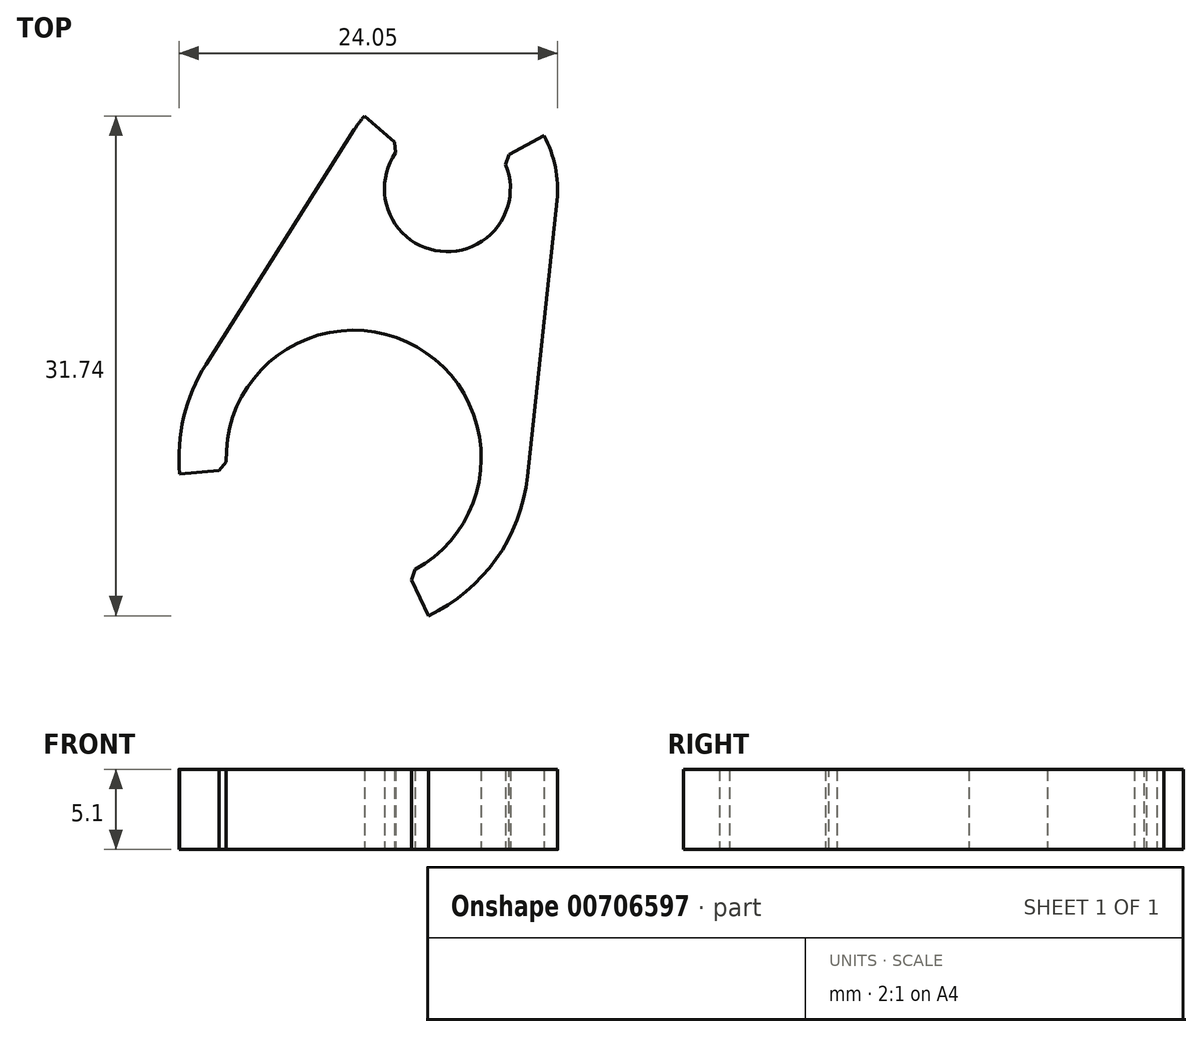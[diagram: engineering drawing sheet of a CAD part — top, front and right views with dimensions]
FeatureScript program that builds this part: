
annotation { "Feature Type Name" : "Feature", "Feature Type Description" : "" }
export const myFeature = defineFeature(function(context is Context, id is Id, definition is map)
    precondition{}
    {
        {
            var Q0;
            Q0=qCreatedBy(makeId("Top.planeOp"),FACE);
            var sketch = newSketch(context, id + "F0", { "sketchPlane" : qUnion([Q0])});
            skCircle(sketch, "E0", {"center": v(0, 0) * mm, "radius": 8.1 * mm});
            skCircle(sketch, "E1", {"center": v(0, 0) * mm, "radius": 11.1 * mm});
            skCircle(sketch, "E2", {"center": v(5.95, 17.1) * mm, "radius": 4 * mm});
            skCircle(sketch, "E3", {"center": v(5.95, 17.1) * mm, "radius": 7 * mm});
            skLineSegment(sketch, "E4", {"start": v(0.03, 20.83) * mm, "end": v(-9.38, 5.93) * mm});
            skLineSegment(sketch, "E5", {"start": v(12.9, 16.35) * mm, "end": v(11.04, -1.18) * mm});
            skLineSegment(sketch, "E6", {"start": v(5.95, 17.1) * mm, "end": v(12.08, 20.46) * mm});
            skLineSegment(sketch, "E7", {"start": v(0, 0) * mm, "end": v(-11.05, -1.03) * mm});
            skLineSegment(sketch, "E8", {"start": v(0, 0) * mm, "end": v(4.75, -10.03) * mm});
            skLineSegment(sketch, "E9", {"start": v(5.95, 17.1) * mm, "end": v(0.68, 21.7) * mm});
            skSolve(sketch);
        }
        {
            var Q0;
            {var subQ0=sQuery(id+"F0.wireOp",EDGE,"E4");Q0=makeQuery(id+"F0.imprint","IMPRINT",FACE,{"disambiguationData":[TD([[makeQuery(id+"F0.imprint","IMPRINT",EDGE,{"derivedFrom":subQ0}),1.0]])]});}
            var Q1;
            {var subQ5=sQuery(id+"F0.wireOp",EDGE,"E7");var subQ8=sQuery(id+"F0.wireOp",EDGE,"E0");var subQ9=makeQuery(id+"F0.imprint","INTERSECT",VERTEX,{"derivedFrom":[subQ8,subQ5]});Q1=makeQuery(id+"F0.imprint","IMPRINT",FACE,{"disambiguationData":[TD([[makeQuery(id+"F0.imprint","IMPRINT",EDGE,{"disambiguationData":[TD([[subQ9,1.0]])],"derivedFrom":subQ8}),-1.0]])]});}
            var Q2;
            {var subQ0=sQuery(id+"F0.wireOp",EDGE,"E5");Q2=makeQuery(id+"F0.imprint","IMPRINT",FACE,{"disambiguationData":[TD([[makeQuery(id+"F0.imprint","IMPRINT",EDGE,{"derivedFrom":subQ0}),-1.0]])]});}
            var Q3;
            {var subQ5=sQuery(id+"F0.wireOp",EDGE,"E2");var subQ8=sQuery(id+"F0.wireOp",EDGE,"E6");var subQ9=makeQuery(id+"F0.imprint","INTERSECT",VERTEX,{"derivedFrom":[subQ5,subQ8]});Q3=makeQuery(id+"F0.imprint","IMPRINT",FACE,{"disambiguationData":[TD([[makeQuery(id+"F0.imprint","IMPRINT",EDGE,{"disambiguationData":[TD([[subQ9,1.0]])],"derivedFrom":subQ5}),-1.0]])]});}
            extrude(context, id + "F1", {"entities" : qUnion([Q0, Q1, Q2, Q3]), "depth" : 5.1 * mm, "offsetDistance" : 25 * mm});
        }
        {
            var Q0;
            Q0=makeQuery(id+"F1.opExtrude","SWEPT_EDGE",EDGE,{"disambiguationData":[OSD([sQuery(id+"F0.wireOp",EDGE,"E2"),sQuery(id+"F0.wireOp",EDGE,"E6")])]});
            var Q1;
            Q1=makeQuery(id+"F1.opExtrude","SWEPT_EDGE",EDGE,{"disambiguationData":[OSD([sQuery(id+"F0.wireOp",EDGE,"E2"),sQuery(id+"F0.wireOp",EDGE,"E9")])]});
            var Q2;
            Q2=makeQuery(id+"F1.opExtrude","SWEPT_EDGE",EDGE,{"disambiguationData":[OSD([sQuery(id+"F0.wireOp",EDGE,"E0"),sQuery(id+"F0.wireOp",EDGE,"E8")])]});
            var Q3;
            Q3=makeQuery(id+"F1.opExtrude","SWEPT_EDGE",EDGE,{"disambiguationData":[OSD([sQuery(id+"F0.wireOp",EDGE,"E0"),sQuery(id+"F0.wireOp",EDGE,"E7")])]});
            chamfer(context, id + "F2", {"entities" : qUnion([Q0, Q1, Q2, Q3]), "width" : 0.5 * mm, "tangentPropagation" : true});
        }
    });
